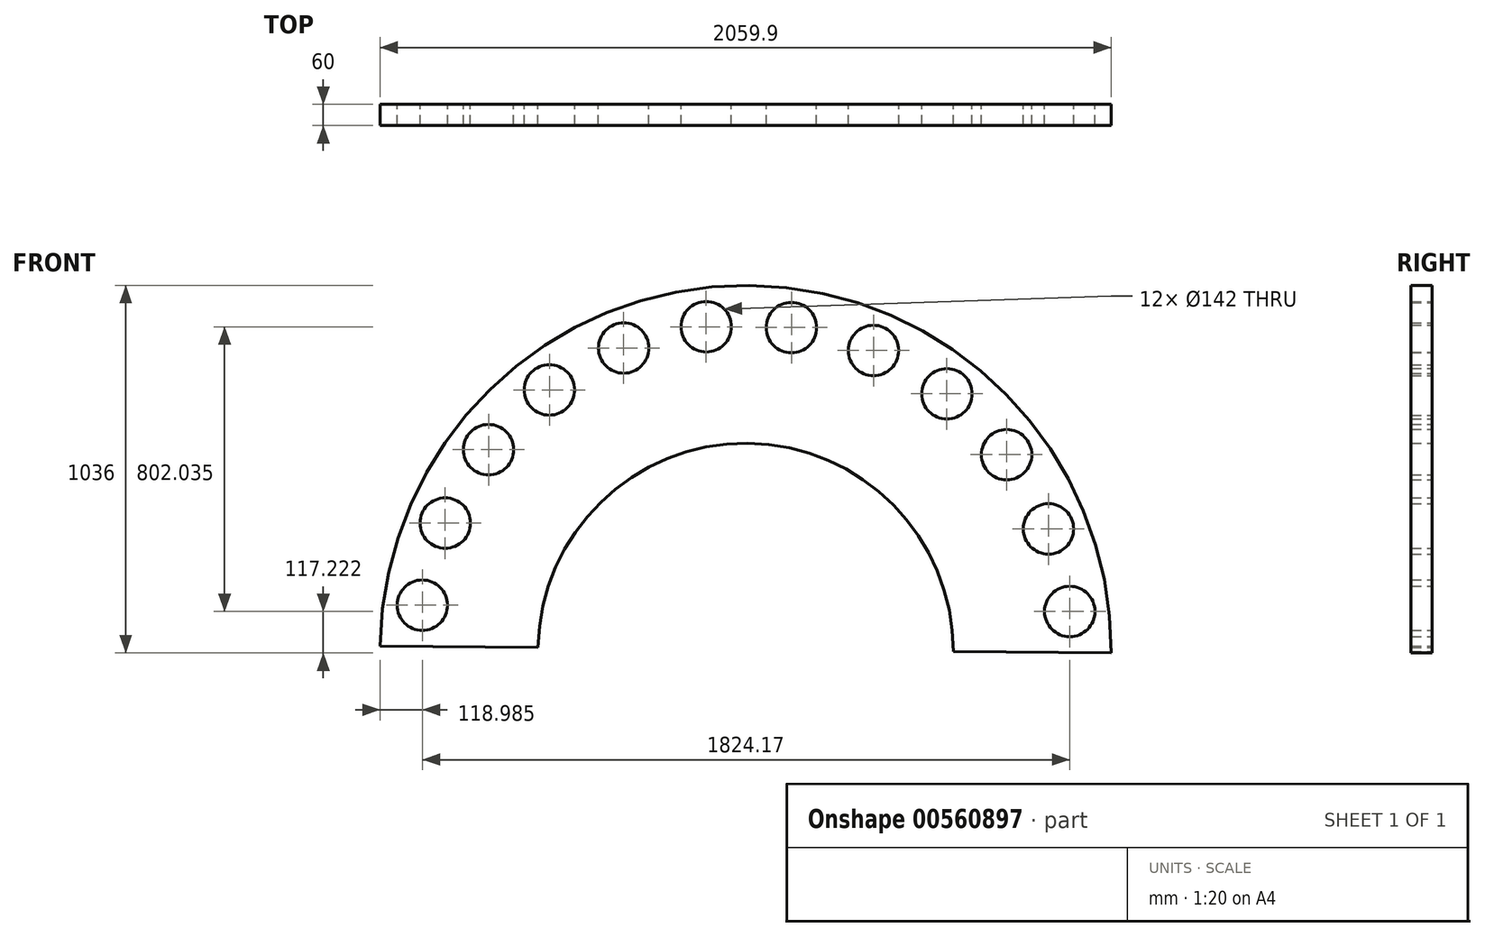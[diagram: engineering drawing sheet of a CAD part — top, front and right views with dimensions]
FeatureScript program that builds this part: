
annotation { "Feature Type Name" : "Feature", "Feature Type Description" : "" }
export const myFeature = defineFeature(function(context is Context, id is Id, definition is map)
    precondition{}
    {
        {
            var Q0;
            Q0=qCreatedBy(makeId("Front.planeOp"),FACE);
            var sketch = newSketch(context, id + "F0", { "sketchPlane" : qUnion([Q0])});
            skArc(sketch, "E0", {"start": v(355.92, 91.62) * mm, "mid": v(-223.4, 678.28) * mm, "end": v(-814, 102.99) * mm});
            skLineSegment(sketch, "E1", {"start": v(-814, 102.99) * mm, "end": v(355.92, 91.62) * mm, "construction": true});
            skArc(sketch, "E2", {"start": v(-1258.98, 107.3) * mm, "mid": v(-219.07, 1123.25) * mm, "end": v(800.9, 87.3) * mm});
            skLineSegment(sketch, "E3", {"start": v(-1258.98, 107.3) * mm, "end": v(800.9, 87.3) * mm, "construction": true});
            skLineSegment(sketch, "E4", {"start": v(-1258.98, 107.3) * mm, "end": v(-814, 102.99) * mm});
            skLineSegment(sketch, "E5", {"start": v(355.92, 91.62) * mm, "end": v(800.9, 87.3) * mm});
            skCircle(sketch, "E6", {"center": v(-229.08, 93.3) * mm, "radius": 920 * mm, "construction": true});
            skCircle(sketch, "E7", {"center": v(-1140, 222.24) * mm, "radius": 71 * mm});
            skLineSegment(sketch, "E8", {"start": v(-229.08, 93.3) * mm, "end": v(-1140, 222.24) * mm, "construction": true});
            skLineSegment(sketch, "E9", {"start": v(-229.08, 93.3) * mm, "end": v(-1448.27, 105.15) * mm, "construction": true});
            skPoint(sketch, "E9.endSnap0", {"position": v(-1036.49, 105.15) * mm});
            skCircle(sketch, "E10.1.0", {"center": v(-1075.58, 453.61) * mm, "radius": 71 * mm});
            skCircle(sketch, "E10.2.0", {"center": v(-953.49, 660.43) * mm, "radius": 71 * mm});
            skCircle(sketch, "E10.3.0", {"center": v(-782.02, 828.6) * mm, "radius": 71 * mm});
            skCircle(sketch, "E10.4.0", {"center": v(-572.87, 946.65) * mm, "radius": 71 * mm});
            skCircle(sketch, "E10.5.0", {"center": v(-340.3, 1006.56) * mm, "radius": 71 * mm});
            skCircle(sketch, "E10.6.0", {"center": v(-100.14, 1004.22) * mm, "radius": 71 * mm});
            skCircle(sketch, "E10.7.0", {"center": v(131.23, 939.81) * mm, "radius": 71 * mm});
            skCircle(sketch, "E10.8.0", {"center": v(338.05, 817.71) * mm, "radius": 71 * mm});
            skCircle(sketch, "E10.9.0", {"center": v(506.22, 646.25) * mm, "radius": 71 * mm});
            skCircle(sketch, "E10.10.0", {"center": v(624.27, 437.1) * mm, "radius": 71 * mm});
            skCircle(sketch, "E10.11.0", {"center": v(684.18, 204.52) * mm, "radius": 71 * mm});
            skLineSegment(sketch, "E10.anchor2", {"start": v(-229.08, 93.3) * mm, "end": v(684.18, 204.52) * mm, "construction": true});
            skLineSegment(sketch, "E11", {"start": v(-229.08, 93.3) * mm, "end": v(9375.58, 0) * mm, "construction": true});
            skSolve(sketch);
        }
        {
            var Q0;
            Q0=qSketchRegion(id+"F0",true);
            extrude(context, id + "F1", {"entities" : qUnion([Q0]), "depth" : 60 * mm, "offsetDistance" : 25 * mm});
        }
    });
